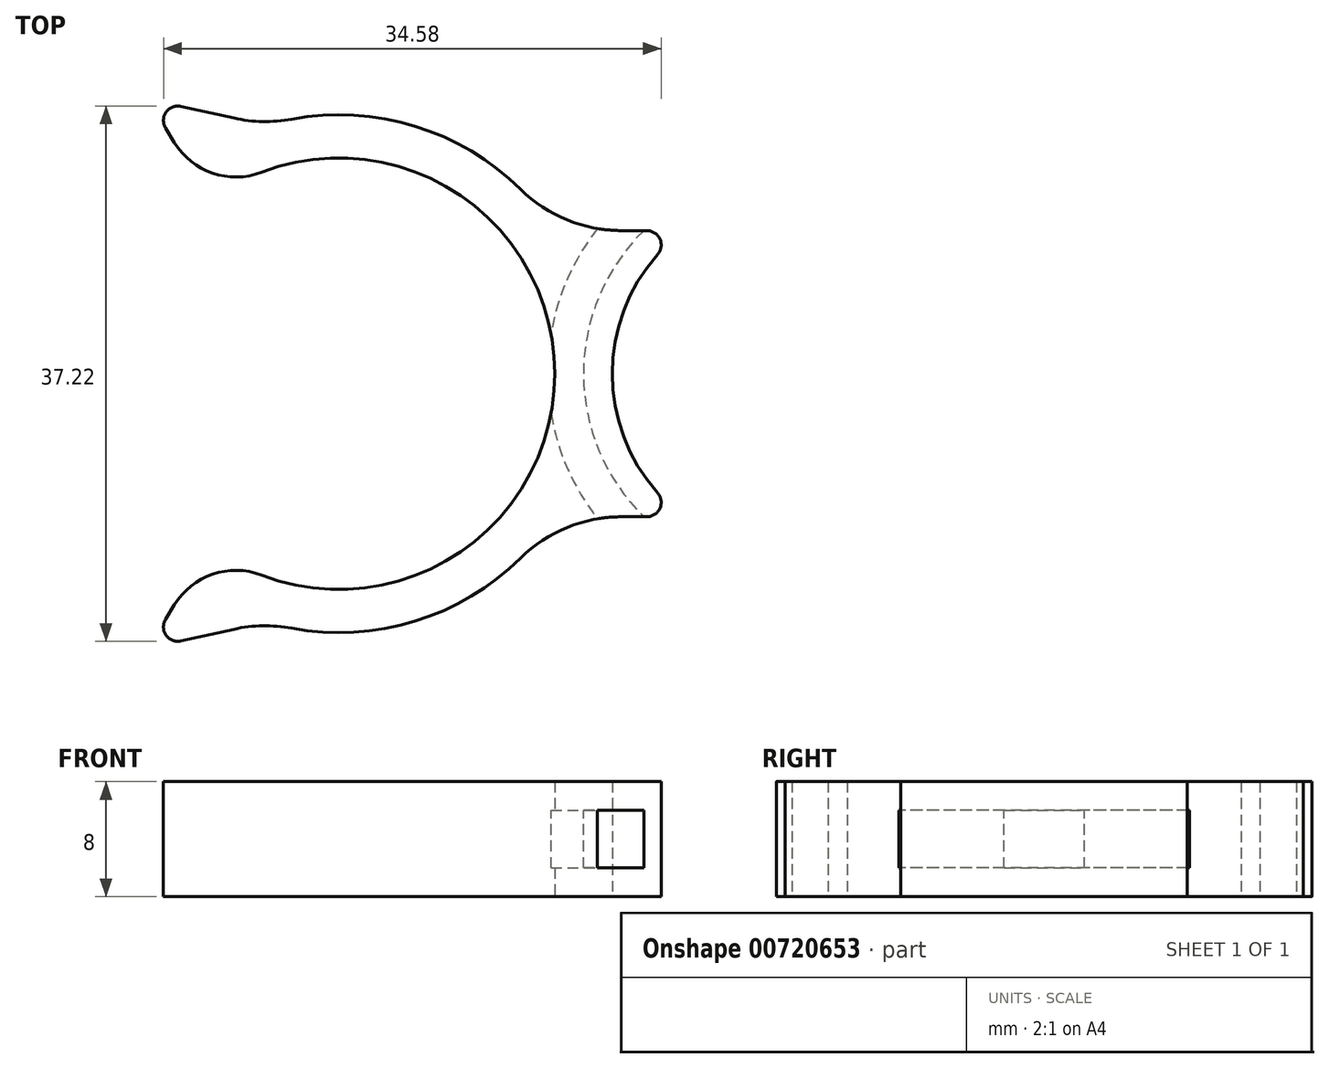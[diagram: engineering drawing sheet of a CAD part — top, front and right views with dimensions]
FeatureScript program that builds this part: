
annotation { "Feature Type Name" : "Feature", "Feature Type Description" : "" }
export const myFeature = defineFeature(function(context is Context, id is Id, definition is map)
    precondition{}
    {
        {
            var Q0;
            Q0=qCreatedBy(makeId("Top.planeOp"),FACE);
            var sketch = newSketch(context, id + "F0", { "sketchPlane" : qUnion([Q0])});
            skArc(sketch, "E0", {"start": v(-26.9, -12.02) * mm, "mid": v(-2.92, 0) * mm, "end": v(-26.9, 12.02) * mm});
            skArc(sketch, "E1", {"start": v(6.01, 9.95) * mm, "mid": v(1.08, 0) * mm, "end": v(6.01, -9.95) * mm});
            skArc(sketch, "E2", {"start": v(-22.99, -17.27) * mm, "mid": v(-11.75, -16.9) * mm, "end": v(-2.92, -9.95) * mm});
            skLineSegment(sketch, "E3", {"start": v(-17.92, 0) * mm, "end": v(13.58, 0) * mm, "construction": true});
            skPoint(sketch, "E4", {"position": v(-2.17, 0) * mm});
            skLineSegment(sketch, "E5.trimOffspring", {"start": v(-2.93, 0.37) * mm, "end": v(-2.92, 0.36) * mm});
            skLineSegment(sketch, "E6.bottom", {"start": v(6.01, 9.95) * mm, "end": v(-2.92, 9.95) * mm});
            skLineSegment(sketch, "E6.top", {"start": v(6.01, -9.95) * mm, "end": v(-2.92, -9.95) * mm});
            skLineSegment(sketch, "E6.right", {"start": v(-2.92, 0.36) * mm, "end": v(-2.92, -0.16) * mm});
            skLineSegment(sketch, "E7.trimOffspring", {"start": v(-2.92, -0.16) * mm, "end": v(-2.92, -0.16) * mm});
            skArc(sketch, "E8.trimOffspring", {"start": v(-2.92, 9.95) * mm, "mid": v(-11.75, 16.9) * mm, "end": v(-22.99, 17.27) * mm});
            skLineSegment(sketch, "E9", {"start": v(-26.9, 12.02) * mm, "end": v(-31.18, 19.1) * mm});
            skLineSegment(sketch, "E10", {"start": v(-31.18, 19.1) * mm, "end": v(-22.99, 17.27) * mm});
            skLineSegment(sketch, "E11.MirrorCS", {"start": v(-26.9, -12.02) * mm, "end": v(-31.18, -19.1) * mm});
            skLineSegment(sketch, "E12.MirrorCS", {"start": v(-31.18, -19.1) * mm, "end": v(-22.99, -17.27) * mm});
            skSolve(sketch);
        }
        {
            var Q0;
            Q0=qSketchRegion(id+"F0",true);
            extrude(context, id + "F1", {"entities" : qUnion([Q0]), "depth" : 8 * mm, "offsetDistance" : 25 * mm});
        }
        {
            var Q0;
            Q0=makeQuery(id+"F1.opExtrude","SWEPT_EDGE",EDGE,{"disambiguationData":[OSD([sQuery(id+"F0.wireOp",EDGE,"E0"),sQuery(id+"F0.wireOp",EDGE,"MHDpRclH-q2Dj-4ouE-9ryf-v0UQ6AgA5fog")])]});
            var Q1;
            Q1=makeQuery(id+"F1.opExtrude","SWEPT_EDGE",EDGE,{"disambiguationData":[OSD([sQuery(id+"F0.wireOp",EDGE,"E0"),sQuery(id+"F0.wireOp",EDGE,"78308c44-5025-46c9-aef0-875acc5395fe.trimOffspring")])]});
            fillet(context, id + "F2", {"entities" : qUnion([Q0, Q1]), "tangentPropagation" : true, "radius" : 5 * mm, "defaultsChanged" : false, "vertexSettings" : [], "allowEdgeOverflow" : false});
        }
        {
            var Q0;
            Q0=makeQuery(id+"F1.opExtrude","SWEPT_EDGE",EDGE,{"disambiguationData":[OSD([sQuery(id+"F0.wireOp",EDGE,"IWztPc0H-4Czz-cEDn-FhKq-w9oCYmKX9AF6"),sQuery(id+"F0.wireOp",EDGE,"92DBHX5X-K6kR-Upr4-bK9H-dtZGLeEnyNnV")])]});
            var Q1;
            Q1=makeQuery(id+"F1.opExtrude","SWEPT_EDGE",EDGE,{"disambiguationData":[OSD([sQuery(id+"F0.wireOp",EDGE,"IWztPc0H-4Czz-cEDn-FhKq-w9oCYmKX9AF6"),sQuery(id+"F0.wireOp",EDGE,"024c119b-de07-41a7-b339-62df15f0e614.trimOffspring")])]});
            var Q2;
            Q2=makeQuery(id+"F1.opExtrude","SWEPT_EDGE",EDGE,{"disambiguationData":[OSD([sQuery(id+"F0.wireOp",EDGE,"3e003569-1aac-4e3d-9f3d-77501b08c2a10.MirrorCS"),sQuery(id+"F0.wireOp",EDGE,"be3c4033-0644-41de-af03-7eb39c3d72080.MirrorCS")])]});
            var Q3;
            Q3=makeQuery(id+"F1.opExtrude","SWEPT_EDGE",EDGE,{"disambiguationData":[OSD([sQuery(id+"F0.wireOp",EDGE,"MHDpRclH-q2Dj-4ouE-9ryf-v0UQ6AgA5fog"),sQuery(id+"F0.wireOp",EDGE,"Bm5BC6q6-ifkZ-6Eal-UUqP-6c5QV21PyJyv")])]});
            var Q4;
            Q4=makeQuery(id+"F1.opExtrude","SWEPT_EDGE",EDGE,{"disambiguationData":[OSD([sQuery(id+"F0.wireOp",EDGE,"E11.MirrorCS"),sQuery(id+"F0.wireOp",EDGE,"E12.MirrorCS")])]});
            var Q5;
            Q5=makeQuery(id+"F1.opExtrude","SWEPT_EDGE",EDGE,{"disambiguationData":[OSD([sQuery(id+"F0.wireOp",EDGE,"E9"),sQuery(id+"F0.wireOp",EDGE,"E10")])]});
            fillet(context, id + "F3", {"entities" : qUnion([Q0, Q1, Q2, Q3, Q4, Q5]), "tangentPropagation" : true, "radius" : 1 * mm, "defaultsChanged" : false, "vertexSettings" : [], "allowEdgeOverflow" : false});
        }
        {
            var Q0;
            Q0=makeQuery(id+"F1.opExtrude","SWEPT_EDGE",EDGE,{"disambiguationData":[OSD([sQuery(id+"F0.wireOp",EDGE,"E6.bottom"),sQuery(id+"F0.wireOp",EDGE,"E8.trimOffspring")])]});
            var Q1;
            Q1=makeQuery(id+"F1.opExtrude","SWEPT_EDGE",EDGE,{"disambiguationData":[OSD([sQuery(id+"F0.wireOp",EDGE,"E2"),sQuery(id+"F0.wireOp",EDGE,"E6.top")])]});
            var Q2;
            Q2=makeQuery(id+"F1.opExtrude","SWEPT_EDGE",EDGE,{"disambiguationData":[OSD([sQuery(id+"F0.wireOp",EDGE,"E8.trimOffspring"),sQuery(id+"F0.wireOp",EDGE,"E10")])]});
            var Q3;
            Q3=makeQuery(id+"F1.opExtrude","SWEPT_EDGE",EDGE,{"disambiguationData":[OSD([sQuery(id+"F0.wireOp",EDGE,"E2"),sQuery(id+"F0.wireOp",EDGE,"E12.MirrorCS")])]});
            fillet(context, id + "F4", {"entities" : qUnion([Q0, Q1, Q2, Q3]), "tangentPropagation" : true, "radius" : 10 * mm, "defaultsChanged" : false, "vertexSettings" : [], "allowEdgeOverflow" : false});
        }
        {
            var Q0;
            Q0=makeQuery(id+"F1.opExtrude","CAP_FACE",FACE,{"disambiguationData":[OSD([sQuery(id+"F0.wireOp",EDGE,"E0"),sQuery(id+"F0.wireOp",EDGE,"E1"),sQuery(id+"F0.wireOp",EDGE,"E2"),sQuery(id+"F0.wireOp",EDGE,"MHDpRclH-q2Dj-4ouE-9ryf-v0UQ6AgA5fog"),sQuery(id+"F0.wireOp",EDGE,"78308c44-5025-46c9-aef0-875acc5395fe.trimOffspring"),sQuery(id+"F0.wireOp",EDGE,"E6.bottom"),sQuery(id+"F0.wireOp",EDGE,"E6.top"),sQuery(id+"F0.wireOp",EDGE,"E8.trimOffspring")])],"isStart":false});
            cPlane(context, id + "F5", {"entities" : qUnion([Q0]), "cplaneType" : CPlaneType.OFFSET, "offset" : 2 * mm, "oppositeDirection" : true, "width" : 150 * mm, "height" : 150 * mm});
        }
        {
            var Q0;
            Q0=qCreatedBy(id+"F5.planeOp",FACE);
            var sketch = newSketch(context, id + "F6", { "sketchPlane" : qUnion([Q0])});
            skArc(sketch, "E13", {"start": v(7.5, 12.78) * mm, "mid": v(-0.77, -2.02) * mm, "end": v(11.4, -13.81) * mm});
            skArc(sketch, "E14", {"start": v(2.7, 12.78) * mm, "mid": v(-3.4, -0.89) * mm, "end": v(4.13, -13.81) * mm});
            skLineSegment(sketch, "E15", {"start": v(2.7, 12.78) * mm, "end": v(7.5, 12.78) * mm});
            skLineSegment(sketch, "E16", {"start": v(11.4, -13.81) * mm, "end": v(4.13, -13.81) * mm});
            skSolve(sketch);
        }
        {
            var Q0;
            Q0=qSketchRegion(id+"F6",true);
            extrude(context, id + "F7", {"entities" : qUnion([Q0]), "operationType" : NewBodyOperationType.REMOVE, "oppositeDirection" : true, "depth" : 4 * mm, "offsetDistance" : 25 * mm});
        }
        {
            var Q0;
            Q0=makeQuery(id+"F1.opExtrude","SWEPT_EDGE",EDGE,{"disambiguationData":[OSD([sQuery(id+"F0.wireOp",EDGE,"E1"),sQuery(id+"F0.wireOp",EDGE,"E6.bottom")])]});
            var Q1;
            Q1=makeQuery(id+"F1.opExtrude","SWEPT_EDGE",EDGE,{"disambiguationData":[OSD([sQuery(id+"F0.wireOp",EDGE,"E1"),sQuery(id+"F0.wireOp",EDGE,"E6.top")])]});
            fillet(context, id + "F8", {"entities" : qUnion([Q0, Q1]), "tangentPropagation" : true, "radius" : 1 * mm, "defaultsChanged" : false, "vertexSettings" : [], "allowEdgeOverflow" : false});
        }
    });
